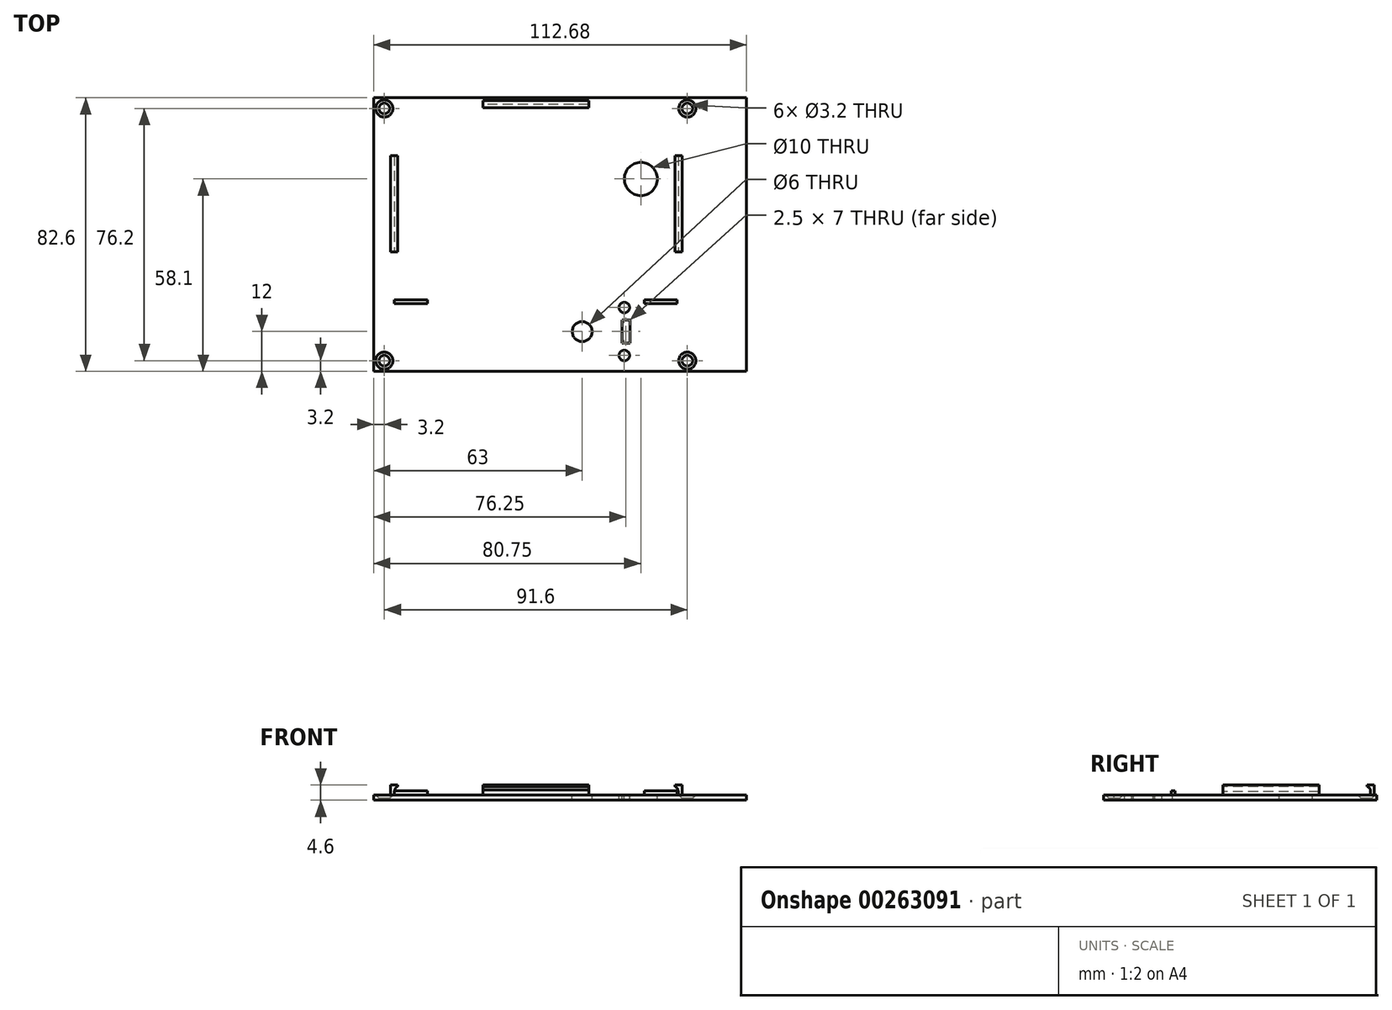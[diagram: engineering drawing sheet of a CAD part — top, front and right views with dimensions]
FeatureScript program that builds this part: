
annotation { "Feature Type Name" : "Feature", "Feature Type Description" : "" }
export const myFeature = defineFeature(function(context is Context, id is Id, definition is map)
    precondition{}
    {
        {
            var Q0;
            Q0=qCreatedBy(makeId("Top.planeOp"),FACE);
            var sketch = newSketch(context, id + "F0", { "sketchPlane" : qUnion([Q0])});
            skLineSegment(sketch, "E0.bottom", {"start": v(0, 0) * mm, "end": v(112.68, 0) * mm});
            skLineSegment(sketch, "E0.top", {"start": v(0, 82.6) * mm, "end": v(112.68, 82.6) * mm});
            skLineSegment(sketch, "E0.left", {"start": v(0, 0) * mm, "end": v(0, 82.6) * mm});
            skLineSegment(sketch, "E0.right", {"start": v(112.68, 0) * mm, "end": v(112.68, 82.6) * mm});
            skLineSegment(sketch, "E1.bottom", {"start": v(3.2, 79.4) * mm, "end": v(94.8, 79.4) * mm, "construction": true});
            skLineSegment(sketch, "E1.top", {"start": v(3.2, 3.2) * mm, "end": v(94.8, 3.2) * mm, "construction": true});
            skLineSegment(sketch, "E1.left", {"start": v(3.2, 79.4) * mm, "end": v(3.2, 3.2) * mm, "construction": true});
            skLineSegment(sketch, "E1.right", {"start": v(94.8, 79.4) * mm, "end": v(94.8, 3.2) * mm, "construction": true});
            skCircle(sketch, "E2", {"center": v(3.2, 79.4) * mm, "radius": 1.6 * mm});
            skCircle(sketch, "E3", {"center": v(94.8, 79.4) * mm, "radius": 1.6 * mm});
            skCircle(sketch, "E4", {"center": v(94.8, 3.2) * mm, "radius": 1.6 * mm});
            skCircle(sketch, "E5", {"center": v(3.2, 3.2) * mm, "radius": 1.6 * mm});
            skSolve(sketch);
        }
        {
            var Q0;
            Q0=makeQuery(id+"F0.imprint","IMPRINT",FACE,{"disambiguationData":[TD([[makeQuery(id+"F0.imprint","IMPRINT",EDGE,{"derivedFrom":sQuery(id+"F0.wireOp",EDGE,"E0.bottom")}),1.0]])]});
            var sketch = newSketch(context, id + "F1", { "sketchPlane" : qUnion([Q0])});
            skLineSegment(sketch, "E6.bottom", {"start": v(6.25, 80.6) * mm, "end": v(91.75, 80.6) * mm, "construction": true});
            skLineSegment(sketch, "E6.top", {"start": v(6.25, 21.6) * mm, "end": v(91.75, 21.6) * mm, "construction": true});
            skLineSegment(sketch, "E6.left", {"start": v(6.25, 80.6) * mm, "end": v(6.25, 21.6) * mm, "construction": true});
            skLineSegment(sketch, "E6.right", {"start": v(91.75, 80.6) * mm, "end": v(91.75, 21.6) * mm, "construction": true});
            skCircle(sketch, "E7", {"center": v(80.75, 58.1) * mm, "radius": 5 * mm});
            skLineSegment(sketch, "E8", {"start": v(49, 80.6) * mm, "end": v(49, 21.6) * mm, "construction": true});
            skLineSegment(sketch, "E9.bottom", {"start": v(6.25, 21.6) * mm, "end": v(16.25, 21.6) * mm});
            skLineSegment(sketch, "E9.top", {"start": v(6.25, 20.4) * mm, "end": v(16.25, 20.4) * mm});
            skLineSegment(sketch, "E9.left", {"start": v(6.25, 21.6) * mm, "end": v(6.25, 20.4) * mm});
            skLineSegment(sketch, "E9.right", {"start": v(16.25, 21.6) * mm, "end": v(16.25, 20.4) * mm});
            skLineSegment(sketch, "E10.bottom", {"start": v(91.75, 21.6) * mm, "end": v(81.75, 21.6) * mm});
            skLineSegment(sketch, "E10.top", {"start": v(91.75, 20.4) * mm, "end": v(81.75, 20.4) * mm});
            skLineSegment(sketch, "E10.left", {"start": v(91.75, 21.6) * mm, "end": v(91.75, 20.4) * mm});
            skLineSegment(sketch, "E10.right", {"start": v(81.75, 21.6) * mm, "end": v(81.75, 20.4) * mm});
            skSolve(sketch);
        }
        {
            var Q0;
            Q0=makeQuery(id+"F0.imprint","IMPRINT",FACE,{"disambiguationData":[TD([[makeQuery(id+"F0.imprint","IMPRINT",EDGE,{"derivedFrom":sQuery(id+"F0.wireOp",EDGE,"E0.bottom")}),1.0]])]});
            var sketch = newSketch(context, id + "F2", { "sketchPlane" : qUnion([Q0])});
            skLineSegment(sketch, "E11.bottom", {"start": v(53.5, 22.5) * mm, "end": v(82.5, 22.5) * mm, "construction": true});
            skLineSegment(sketch, "E11.top", {"start": v(53.5, 1.5) * mm, "end": v(82.5, 1.5) * mm, "construction": true});
            skLineSegment(sketch, "E11.left", {"start": v(53.5, 22.5) * mm, "end": v(53.5, 1.5) * mm, "construction": true});
            skLineSegment(sketch, "E11.right", {"start": v(82.5, 22.5) * mm, "end": v(82.5, 1.5) * mm, "construction": true});
            skCircle(sketch, "E12", {"center": v(75.75, 19.25) * mm, "radius": 1.6 * mm});
            skCircle(sketch, "E13", {"center": v(75.75, 4.75) * mm, "radius": 1.6 * mm});
            skCircle(sketch, "E14", {"center": v(63, 12) * mm, "radius": 3 * mm});
            skLineSegment(sketch, "E15.bottom", {"start": v(75, 15.5) * mm, "end": v(77.5, 15.5) * mm});
            skLineSegment(sketch, "E15.top", {"start": v(75, 8.5) * mm, "end": v(77.5, 8.5) * mm});
            skLineSegment(sketch, "E15.left", {"start": v(75, 15.5) * mm, "end": v(75, 8.5) * mm});
            skLineSegment(sketch, "E15.right", {"start": v(77.5, 15.5) * mm, "end": v(77.5, 8.5) * mm});
            skSolve(sketch);
        }
        {
            var Q0;
            Q0=makeQuery(id+"F0.imprint","IMPRINT",FACE,{"disambiguationData":[TD([[makeQuery(id+"F0.imprint","IMPRINT",EDGE,{"derivedFrom":sQuery(id+"F0.wireOp",EDGE,"E0.bottom")}),1.0]])]});
            extrude(context, id + "F3", {"entities" : qUnion([Q0]), "oppositeDirection" : true, "depth" : 1.6 * mm});
        }
        {
            var Q0;
            Q0=makeQuery(id+"F1.imprint","IMPRINT",FACE,{"disambiguationData":[TD([[makeQuery(id+"F1.imprint","IMPRINT",EDGE,{"derivedFrom":sQuery(id+"F1.wireOp",EDGE,"E7")}),1.0]])]});
            extrude(context, id + "F4", {"entities" : qUnion([Q0]), "operationType" : NewBodyOperationType.REMOVE, "endBound" : BoundingType.THROUGH_ALL, "oppositeDirection" : true, "depth" : 25 * mm});
        }
        {
            var Q0;
            Q0=makeQuery(id+"F2.imprint","IMPRINT",FACE,{"disambiguationData":[TD([[makeQuery(id+"F2.imprint","IMPRINT",EDGE,{"derivedFrom":sQuery(id+"F2.wireOp",EDGE,"E13")}),1.0]])]});
            var Q1;
            Q1=makeQuery(id+"F2.imprint","IMPRINT",FACE,{"disambiguationData":[TD([[makeQuery(id+"F2.imprint","IMPRINT",EDGE,{"derivedFrom":sQuery(id+"F2.wireOp",EDGE,"E14")}),1.0]])]});
            var Q2;
            Q2=makeQuery(id+"F2.imprint","IMPRINT",FACE,{"disambiguationData":[TD([[makeQuery(id+"F2.imprint","IMPRINT",EDGE,{"derivedFrom":sQuery(id+"F2.wireOp",EDGE,"E15.bottom")}),-1.0]])]});
            var Q3;
            Q3=makeQuery(id+"F2.imprint","IMPRINT",FACE,{"disambiguationData":[TD([[makeQuery(id+"F2.imprint","IMPRINT",EDGE,{"derivedFrom":sQuery(id+"F2.wireOp",EDGE,"E12")}),1.0]])]});
            extrude(context, id + "F5", {"entities" : qUnion([Q0, Q1, Q2, Q3]), "operationType" : NewBodyOperationType.REMOVE, "endBound" : BoundingType.THROUGH_ALL, "oppositeDirection" : true, "depth" : 25 * mm});
        }
        {
            var Q0;
            Q0=qCreatedBy(makeId("Front.planeOp"),FACE);
            var sketch = newSketch(context, id + "F6", { "sketchPlane" : qUnion([Q0])});
            skLineSegment(sketch, "E16", {"start": v(6.25, 0) * mm, "end": v(5.05, 0) * mm});
            skLineSegment(sketch, "E17.bottom", {"start": v(5.05, 0) * mm, "end": v(6.25, 0) * mm});
            skLineSegment(sketch, "E17.top", {"start": v(5.05, 0) * mm, "end": v(6.25, 0) * mm});
            skLineSegment(sketch, "E17.left", {"start": v(5.05, 0) * mm, "end": v(5.05, 0) * mm});
            skLineSegment(sketch, "E17.right", {"start": v(6.25, 0) * mm, "end": v(6.25, 0) * mm});
            skLineSegment(sketch, "E18.bottom", {"start": v(6.25, 3) * mm, "end": v(5.05, 3) * mm});
            skLineSegment(sketch, "E18.left", {"start": v(6.25, 3) * mm, "end": v(6.25, 0) * mm});
            skLineSegment(sketch, "E18.right", {"start": v(5.05, 3) * mm, "end": v(5.05, 0) * mm});
            skLineSegment(sketch, "E19", {"start": v(6.25, 3) * mm, "end": v(7.25, 3) * mm});
            skLineSegment(sketch, "E20", {"start": v(7.25, 3) * mm, "end": v(7.25, 2.5) * mm});
            skFitSpline(sketch, "E21", {"points": [v(7.25, 2.5) * mm, v(6.25, 0) * mm], "startDerivative": vector(-3.78, -0.96) * mm, "endDerivative": vector(0, -0.48) * mm});
            skLineSegment(sketch, "E22", {"start": v(49.15, 0) * mm, "end": v(49.15, 10.87) * mm, "construction": true});
            skLineSegment(sketch, "E23.MirrorCS", {"start": v(92.05, 3) * mm, "end": v(93.25, 3) * mm});
            skLineSegment(sketch, "E24.MirrorCS", {"start": v(92.05, 3) * mm, "end": v(91.05, 3) * mm});
            skLineSegment(sketch, "E25.MirrorCS", {"start": v(91.05, 3) * mm, "end": v(91.05, 2.5) * mm});
            skLineSegment(sketch, "E26.MirrorCS", {"start": v(92.05, 3) * mm, "end": v(92.05, 0) * mm});
            skFitSpline(sketch, "E27.MirrorCS", {"points": [v(91.05, 2.5) * mm, v(92.05, 0) * mm], "startDerivative": vector(3.78, -0.96) * mm, "endDerivative": vector(0, -0.48) * mm});
            skLineSegment(sketch, "E28.MirrorCS", {"start": v(92.05, 0) * mm, "end": v(93.25, 0) * mm});
            skLineSegment(sketch, "E29.MirrorCS", {"start": v(93.25, 3) * mm, "end": v(93.25, 0) * mm});
            skSolve(sketch);
        }
        {
            var Q0;
            Q0 = qSketchRegion(id + "F6", true);
            extrude(context, id + "F7", {"entities" : qUnion([Q0]), "operationType" : NewBodyOperationType.ADD, "oppositeDirection" : true, "depth" : 65.1 * mm, "hasSecondDirection" : true, "secondDirectionOppositeDirection" : true, "secondDirectionDepth" : 36.1 * mm});
        }
        {
            var Q0;
            Q0=qCreatedBy(makeId("Right.planeOp"),FACE);
            var sketch = newSketch(context, id + "F8", { "sketchPlane" : qUnion([Q0])});
            skLineSegment(sketch, "E30.bottom", {"start": v(80.62, 0) * mm, "end": v(81.82, 0) * mm});
            skLineSegment(sketch, "E30.top", {"start": v(80.62, 3) * mm, "end": v(81.82, 3) * mm});
            skLineSegment(sketch, "E30.left", {"start": v(80.62, 0) * mm, "end": v(80.62, 3) * mm});
            skLineSegment(sketch, "E30.right", {"start": v(81.82, 0) * mm, "end": v(81.82, 3) * mm});
            skLineSegment(sketch, "E31", {"start": v(80.62, 3) * mm, "end": v(79.62, 3) * mm});
            skLineSegment(sketch, "E32", {"start": v(79.62, 3) * mm, "end": v(79.62, 2.5) * mm});
            skFitSpline(sketch, "E33", {"points": [v(79.62, 2.5) * mm, v(80.62, 1.5) * mm, v(80.62, 0) * mm], "startDerivative": vector(3.74, -1.12) * mm, "endDerivative": vector(0, -1.77) * mm});
            skSolve(sketch);
        }
        {
            var Q0;
            Q0 = qSketchRegion(id + "F8", true);
            extrude(context, id + "F9", {"entities" : qUnion([Q0]), "operationType" : NewBodyOperationType.ADD, "depth" : 65 * mm, "hasSecondDirection" : true, "secondDirectionOppositeDirection" : false, "secondDirectionDepth" : 33 * mm});
        }
        {
            var Q0;
            Q0=makeQuery(id+"F1.imprint","IMPRINT",FACE,{"disambiguationData":[TD([[makeQuery(id+"F1.imprint","IMPRINT",EDGE,{"derivedFrom":sQuery(id+"F1.wireOp",EDGE,"E9.bottom")}),-1.0]])]});
            var Q1;
            Q1=makeQuery(id+"F1.imprint","IMPRINT",FACE,{"disambiguationData":[TD([[makeQuery(id+"F1.imprint","IMPRINT",EDGE,{"derivedFrom":sQuery(id+"F1.wireOp",EDGE,"E10.bottom")}),1.0]])]});
            extrude(context, id + "F10", {"entities" : qUnion([Q0, Q1]), "operationType" : NewBodyOperationType.ADD, "depth" : 1.2 * mm});
        }
        {
            var Q0;
            Q0=makeQuery(id+"F3.opExtrude","CAP_EDGE",EDGE,{"disambiguationData":[OSD([sQuery(id+"F0.wireOp",EDGE,"E2")])],"isStart":true});
            var Q1;
            Q1=makeQuery(id+"F3.opExtrude","CAP_EDGE",EDGE,{"disambiguationData":[OSD([sQuery(id+"F0.wireOp",EDGE,"E5")])],"isStart":true});
            var Q2;
            Q2=makeQuery(id+"F5.boolean.opBoolean","COPY",EDGE,{"derivedFrom":makeQuery(id+"F5.opExtrude","CAP_EDGE",EDGE,{"disambiguationData":[OSD([sQuery(id+"F2.wireOp",EDGE,"E13")])],"isStart":true})});
            var Q3;
            Q3=makeQuery(id+"F5.boolean.opBoolean","COPY",EDGE,{"derivedFrom":makeQuery(id+"F5.opExtrude","CAP_EDGE",EDGE,{"disambiguationData":[OSD([sQuery(id+"F2.wireOp",EDGE,"E12")])],"isStart":true})});
            var Q4;
            Q4=makeQuery(id+"F3.opExtrude","CAP_EDGE",EDGE,{"disambiguationData":[OSD([sQuery(id+"F0.wireOp",EDGE,"E4")])],"isStart":true});
            var Q5;
            Q5=makeQuery(id+"F3.opExtrude","CAP_EDGE",EDGE,{"disambiguationData":[OSD([sQuery(id+"F0.wireOp",EDGE,"E3")])],"isStart":true});
            chamfer(context, id + "F11", {"entities" : qUnion([Q0, Q1, Q2, Q3, Q4, Q5]), "width" : 1 * mm, "tangentPropagation" : true});
        }
    });
